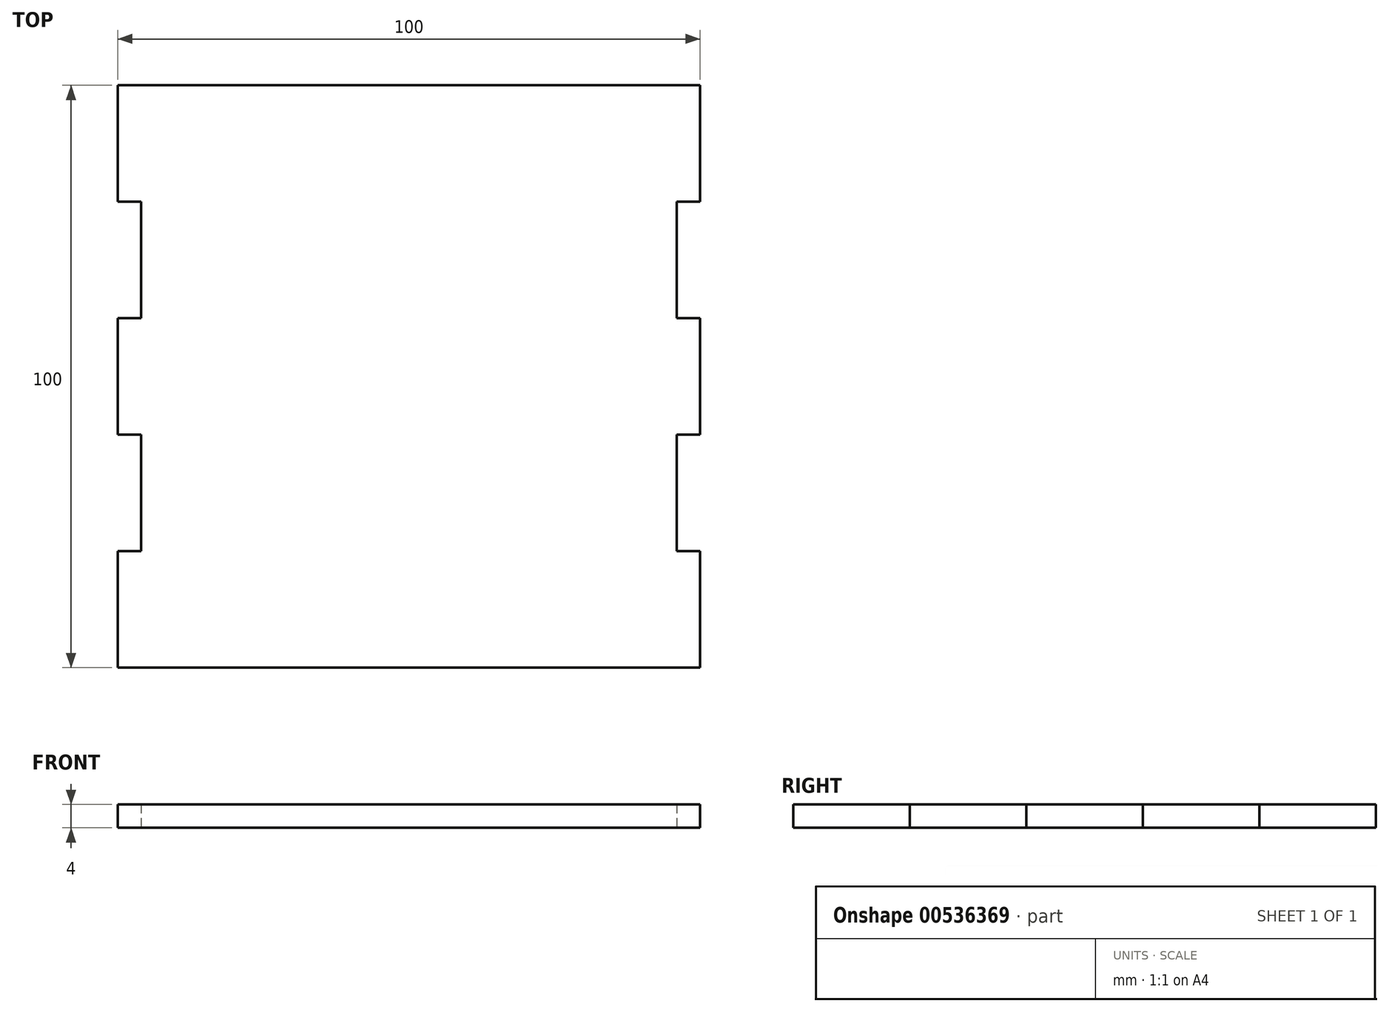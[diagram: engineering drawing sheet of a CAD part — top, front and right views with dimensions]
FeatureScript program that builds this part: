
annotation { "Feature Type Name" : "Feature", "Feature Type Description" : "" }
export const myFeature = defineFeature(function(context is Context, id is Id, definition is map)
    precondition{}
    {
        {
            var Q0;
            Q0=qCreatedBy(makeId("Top.planeOp"),FACE);
            var sketch = newSketch(context, id + "F0", { "sketchPlane" : qUnion([Q0])});
            skLineSegment(sketch, "E0.bottom", {"start": v(-50, -50) * mm, "end": v(50, -50) * mm});
            skLineSegment(sketch, "E0.top", {"start": v(-50, 50) * mm, "end": v(50, 50) * mm});
            skLineSegment(sketch, "E0.left", {"start": v(-50, -50) * mm, "end": v(-50, 50) * mm});
            skLineSegment(sketch, "E0.right", {"start": v(50, -50) * mm, "end": v(50, 50) * mm});
            skPoint(sketch, "E0.middle", {"position": v(0, 0) * mm});
            skLineSegment(sketch, "E1.bottom", {"start": v(-50, 30) * mm, "end": v(-46, 30) * mm});
            skLineSegment(sketch, "E1.top", {"start": v(-50, 10) * mm, "end": v(-46, 10) * mm});
            skLineSegment(sketch, "E1.left", {"start": v(-50, 30) * mm, "end": v(-50, 10) * mm});
            skLineSegment(sketch, "E1.right", {"start": v(-46, 30) * mm, "end": v(-46, 10) * mm});
            skLineSegment(sketch, "E2.bottom", {"start": v(-50, -10) * mm, "end": v(-46, -10) * mm});
            skLineSegment(sketch, "E2.top", {"start": v(-50, -30) * mm, "end": v(-46, -30) * mm});
            skLineSegment(sketch, "E2.left", {"start": v(-50, -10) * mm, "end": v(-50, -30) * mm});
            skLineSegment(sketch, "E2.right", {"start": v(-46, -10) * mm, "end": v(-46, -30) * mm});
            skLineSegment(sketch, "E3.bottom", {"start": v(-30, 50) * mm, "end": v(-10, 50) * mm});
            skLineSegment(sketch, "E3.top", {"start": v(-30, 46) * mm, "end": v(-10, 46) * mm});
            skLineSegment(sketch, "E3.left", {"start": v(-30, 50) * mm, "end": v(-30, 46) * mm});
            skLineSegment(sketch, "E3.right", {"start": v(-10, 50) * mm, "end": v(-10, 46) * mm});
            skLineSegment(sketch, "E4.bottom", {"start": v(10, 50) * mm, "end": v(30, 50) * mm});
            skLineSegment(sketch, "E4.top", {"start": v(10, 46) * mm, "end": v(30, 46) * mm});
            skLineSegment(sketch, "E4.left", {"start": v(10, 50) * mm, "end": v(10, 46) * mm});
            skLineSegment(sketch, "E4.right", {"start": v(30, 50) * mm, "end": v(30, 46) * mm});
            skLineSegment(sketch, "E5.bottom", {"start": v(50, 30) * mm, "end": v(46, 30) * mm});
            skLineSegment(sketch, "E5.top", {"start": v(50, 10) * mm, "end": v(46, 10) * mm});
            skLineSegment(sketch, "E5.left", {"start": v(50, 30) * mm, "end": v(50, 10) * mm});
            skLineSegment(sketch, "E5.right", {"start": v(46, 30) * mm, "end": v(46, 10) * mm});
            skLineSegment(sketch, "E6.bottom", {"start": v(50, -10) * mm, "end": v(46, -10) * mm});
            skLineSegment(sketch, "E6.top", {"start": v(50, -30) * mm, "end": v(46, -30) * mm});
            skLineSegment(sketch, "E6.left", {"start": v(50, -10) * mm, "end": v(50, -30) * mm});
            skLineSegment(sketch, "E6.right", {"start": v(46, -10) * mm, "end": v(46, -30) * mm});
            skLineSegment(sketch, "E7.bottom", {"start": v(-30, -50) * mm, "end": v(-10, -50) * mm});
            skLineSegment(sketch, "E7.top", {"start": v(-30, -46) * mm, "end": v(-10, -46) * mm});
            skLineSegment(sketch, "E7.left", {"start": v(-30, -50) * mm, "end": v(-30, -46) * mm});
            skLineSegment(sketch, "E7.right", {"start": v(-10, -50) * mm, "end": v(-10, -46) * mm});
            skLineSegment(sketch, "E8.bottom", {"start": v(10, -50) * mm, "end": v(30, -50) * mm});
            skLineSegment(sketch, "E8.top", {"start": v(10, -46) * mm, "end": v(30, -46) * mm});
            skLineSegment(sketch, "E8.left", {"start": v(10, -50) * mm, "end": v(10, -46) * mm});
            skLineSegment(sketch, "E8.right", {"start": v(30, -50) * mm, "end": v(30, -46) * mm});
            skSolve(sketch);
        }
        {
            var Q0;
            Q0 = qSketchRegion(id + "F0", true);
            extrude(context, id + "F1", {"entities" : qUnion([Q0]), "depth" : 4 * mm, "offsetDistance" : 25 * mm});
        }
        {
            var Q0;
            Q0=makeQuery(id+"F0.imprint","IMPRINT",FACE,{"disambiguationData":[TD([[makeQuery(id+"F0.imprint","IMPRINT",EDGE,{"derivedFrom":sQuery(id+"F0.wireOp",EDGE,"E1.bottom")}),-1.0]])]});
            var Q1;
            Q1=makeQuery(id+"F0.imprint","IMPRINT",FACE,{"disambiguationData":[TD([[makeQuery(id+"F0.imprint","IMPRINT",EDGE,{"derivedFrom":sQuery(id+"F0.wireOp",EDGE,"E2.bottom")}),-1.0]])]});
            var Q2;
            Q2=makeQuery(id+"F0.imprint","IMPRINT",FACE,{"disambiguationData":[TD([[makeQuery(id+"F0.imprint","IMPRINT",EDGE,{"derivedFrom":sQuery(id+"F0.wireOp",EDGE,"E7.bottom")}),1.0]])]});
            var Q3;
            Q3=makeQuery(id+"F0.imprint","IMPRINT",FACE,{"disambiguationData":[TD([[makeQuery(id+"F0.imprint","IMPRINT",EDGE,{"derivedFrom":sQuery(id+"F0.wireOp",EDGE,"E8.bottom")}),1.0]])]});
            var Q4;
            Q4=makeQuery(id+"F0.imprint","IMPRINT",FACE,{"disambiguationData":[TD([[makeQuery(id+"F0.imprint","IMPRINT",EDGE,{"derivedFrom":sQuery(id+"F0.wireOp",EDGE,"E6.bottom")}),1.0]])]});
            var Q5;
            Q5=makeQuery(id+"F0.imprint","IMPRINT",FACE,{"disambiguationData":[TD([[makeQuery(id+"F0.imprint","IMPRINT",EDGE,{"derivedFrom":sQuery(id+"F0.wireOp",EDGE,"E5.bottom")}),1.0]])]});
            var Q6;
            Q6=makeQuery(id+"F0.imprint","IMPRINT",FACE,{"disambiguationData":[TD([[makeQuery(id+"F0.imprint","IMPRINT",EDGE,{"derivedFrom":sQuery(id+"F0.wireOp",EDGE,"E4.bottom")}),-1.0]])]});
            var Q7;
            Q7=makeQuery(id+"F0.imprint","IMPRINT",FACE,{"disambiguationData":[TD([[makeQuery(id+"F0.imprint","IMPRINT",EDGE,{"derivedFrom":sQuery(id+"F0.wireOp",EDGE,"E3.bottom")}),-1.0]])]});
            extrude(context, id + "F2", {"entities" : qUnion([Q0, Q1, Q2, Q3, Q4, Q5, Q6, Q7]), "operationType" : NewBodyOperationType.REMOVE, "depth" : 4 * mm, "offsetDistance" : 25 * mm});
        }
    });
